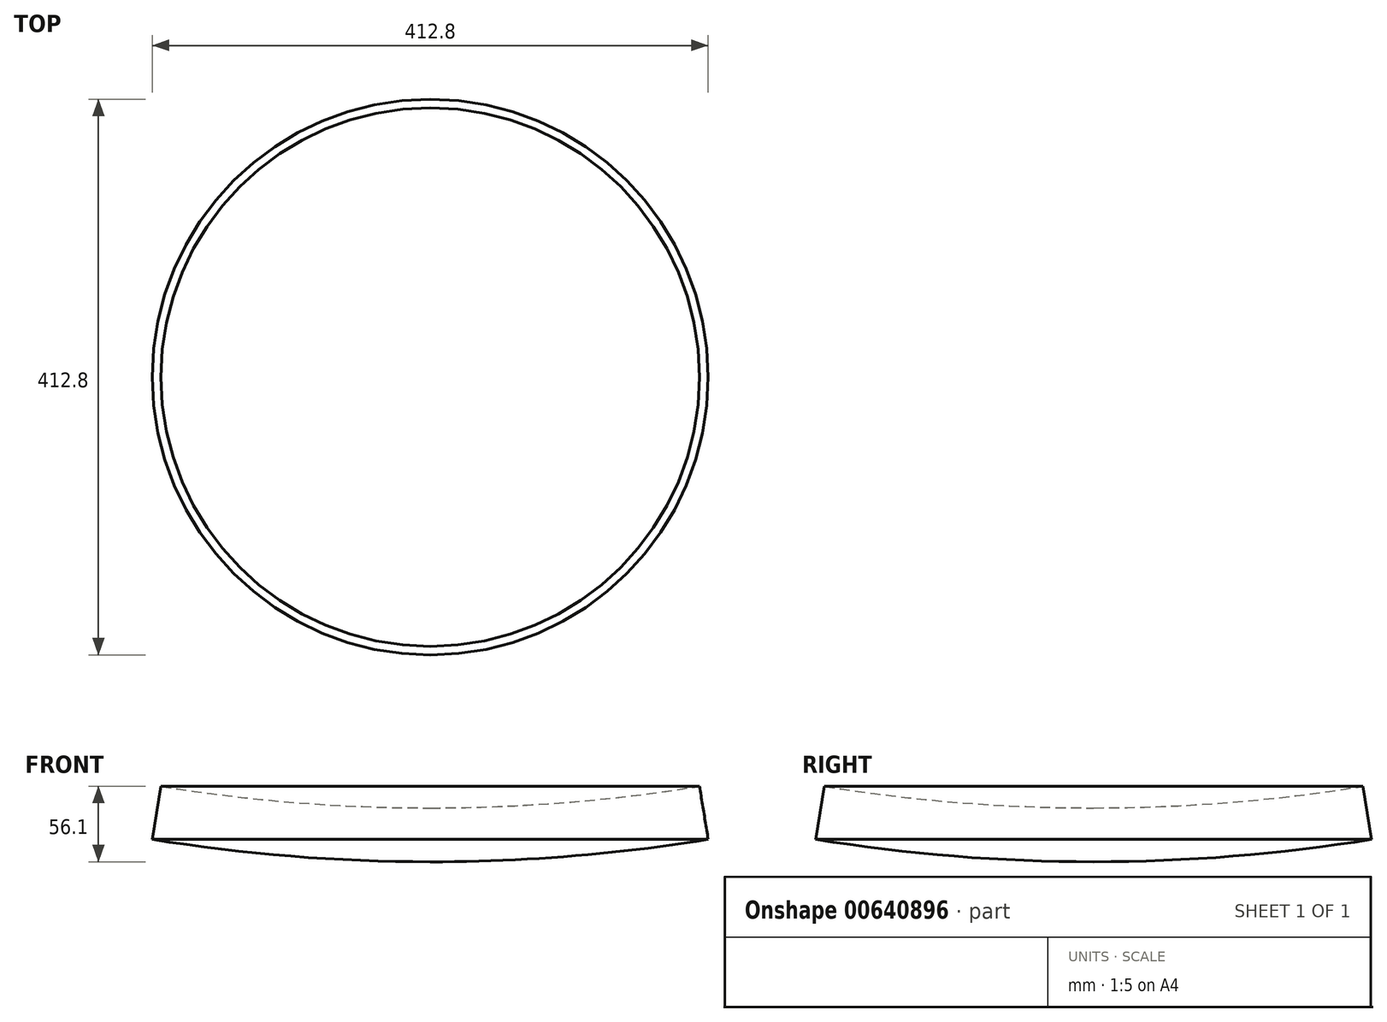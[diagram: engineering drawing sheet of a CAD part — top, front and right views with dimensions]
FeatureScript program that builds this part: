
annotation { "Feature Type Name" : "Feature", "Feature Type Description" : "" }
export const myFeature = defineFeature(function(context is Context, id is Id, definition is map)
    precondition{}
    {
        {
            var Q0;
            Q0=qCreatedBy(makeId("Front.planeOp"),FACE);
            var sketch = newSketch(context, id + "F0", { "sketchPlane" : qUnion([Q0])});
            skArc(sketch, "E0", {"start": v(0, 470) * mm, "mid": v(100.32, 474.03) * mm, "end": v(200, 486.1) * mm});
            skLineSegment(sketch, "E1", {"start": v(0, 1720) * mm, "end": v(0, 0) * mm, "construction": true});
            skLineSegment(sketch, "E2", {"start": v(200, 486.1) * mm, "end": v(206.4, 446.62) * mm});
            skArc(sketch, "E3.0", {"start": v(0, 430) * mm, "mid": v(103.53, 434.16) * mm, "end": v(206.4, 446.62) * mm});
            skLineSegment(sketch, "E4", {"start": v(0, 470) * mm, "end": v(0, 430) * mm});
            skSolve(sketch);
        }
        {
            var Q0;
            Q0 = qSketchRegion(id + "F0", true);
            var Q1;
            Q1=sQuery(id+"F0.wireOp",EDGE,"E1");
            revolve(context, id + "F1", {"entities" : qUnion([Q0]), "axis" : qUnion([Q1]), "revolveType" : RevolveType.FULL});
        }
    });
